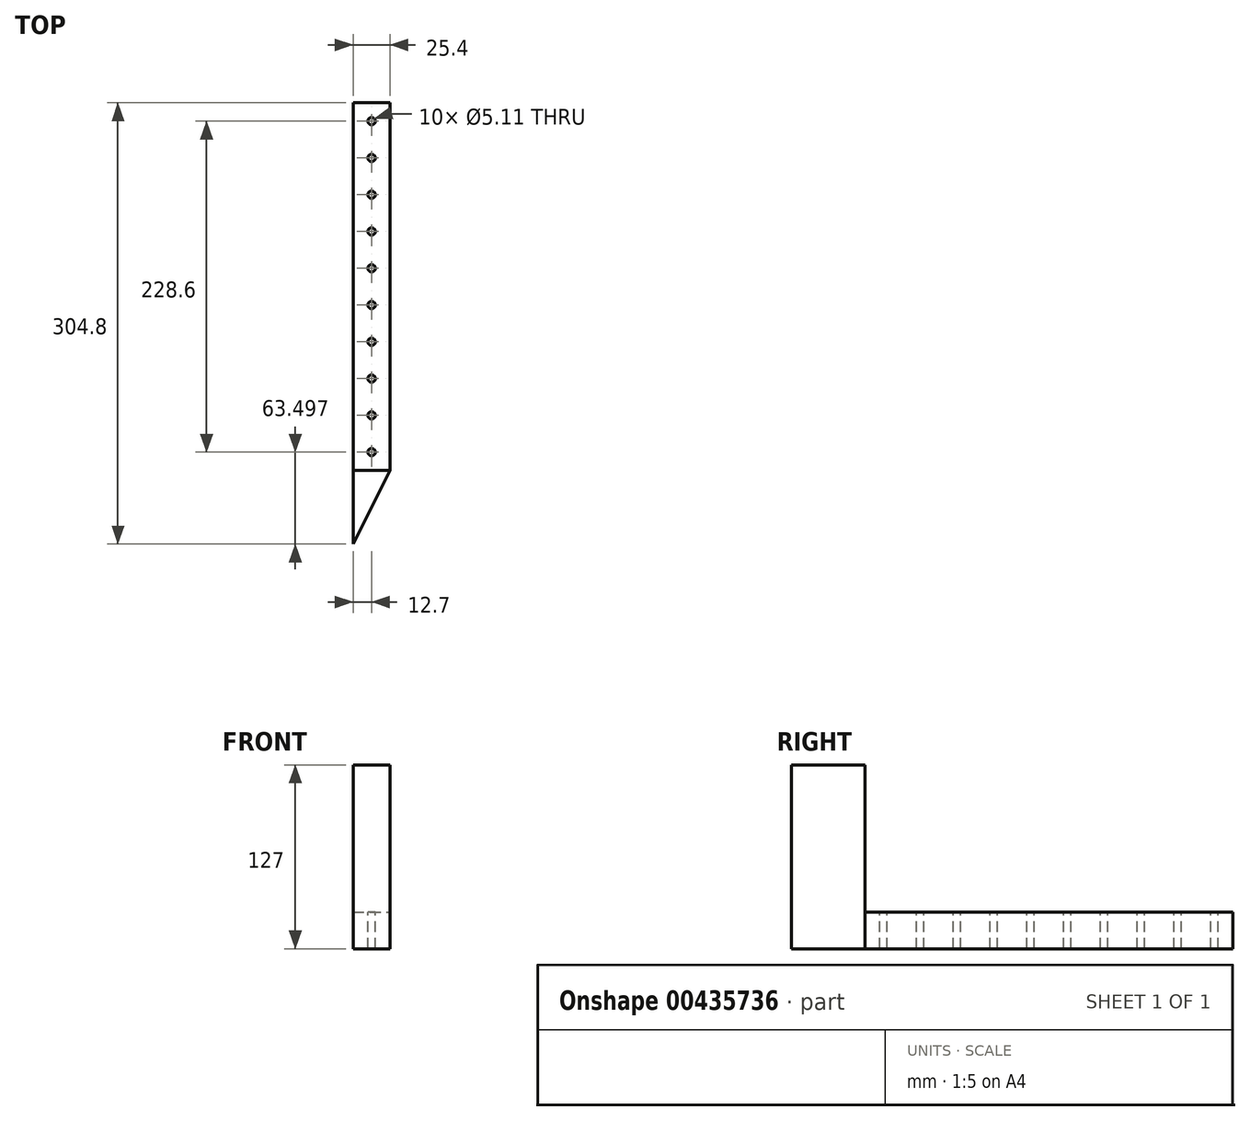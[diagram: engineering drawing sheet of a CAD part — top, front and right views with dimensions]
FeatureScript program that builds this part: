
annotation { "Feature Type Name" : "Feature", "Feature Type Description" : "" }
export const myFeature = defineFeature(function(context is Context, id is Id, definition is map)
    precondition{}
    {
        {
            var Q0;
            Q0=qCreatedBy(makeId("Top.planeOp"),FACE);
            var sketch = newSketch(context, id + "F0", { "sketchPlane" : qUnion([Q0])});
            skLineSegment(sketch, "E0.bottom", {"start": v(-56.37, 216.77) * mm, "end": v(-30.97, 216.77) * mm});
            skLineSegment(sketch, "E0.top", {"start": v(-56.37, -37.23) * mm, "end": v(-30.97, -37.23) * mm});
            skLineSegment(sketch, "E0.left", {"start": v(-56.37, 216.77) * mm, "end": v(-56.37, -37.23) * mm});
            skLineSegment(sketch, "E0.right", {"start": v(-30.97, 216.77) * mm, "end": v(-30.97, -37.23) * mm});
            skLineSegment(sketch, "E1", {"start": v(-56.37, -37.23) * mm, "end": v(-56.37, -88.03) * mm});
            skLineSegment(sketch, "E2", {"start": v(-56.37, -88.03) * mm, "end": v(-30.97, -37.23) * mm});
            skSolve(sketch);
        }
        {
            var Q0;
            Q0=makeQuery(id+"F0.imprint","IMPRINT",FACE,{"disambiguationData":[TD([[makeQuery(id+"F0.imprint","IMPRINT",EDGE,{"derivedFrom":sQuery(id+"F0.wireOp",EDGE,"E0.bottom")}),-1.0]])]});
            extrude(context, id + "F1", {"entities" : qUnion([Q0]), "depth" : 25.4 * mm});
        }
        {
            var Q0;
            Q0=makeQuery(id+"F0.imprint","IMPRINT",FACE,{"disambiguationData":[TD([[makeQuery(id+"F0.imprint","IMPRINT",EDGE,{"derivedFrom":sQuery(id+"F0.wireOp",EDGE,"E0.top")}),-1.0]])]});
            extrude(context, id + "F2", {"entities" : qUnion([Q0]), "operationType" : NewBodyOperationType.ADD, "depth" : 127 * mm});
        }
        {
            var Q0;
            Q0=makeQuery(id+"F1.opExtrude","CAP_FACE",FACE,{"disambiguationData":[OSD([sQuery(id+"F0.wireOp",EDGE,"E0.bottom"),sQuery(id+"F0.wireOp",EDGE,"E0.top"),sQuery(id+"F0.wireOp",EDGE,"E0.left"),sQuery(id+"F0.wireOp",EDGE,"E0.right")])],"isStart":false});
            var sketch = newSketch(context, id + "F3", { "sketchPlane" : qUnion([Q0])});
            skCircle(sketch, "E3", {"center": v(-43.67, 204.07) * mm, "radius": 2.55 * mm});
            skCircle(sketch, "E4.0.1.0", {"center": v(-43.67, 178.67) * mm, "radius": 2.55 * mm});
            skCircle(sketch, "E4.0.2.0", {"center": v(-43.67, 153.27) * mm, "radius": 2.55 * mm});
            skCircle(sketch, "E4.0.3.0", {"center": v(-43.67, 127.87) * mm, "radius": 2.55 * mm});
            skCircle(sketch, "E4.0.4.0", {"center": v(-43.67, 102.47) * mm, "radius": 2.55 * mm});
            skCircle(sketch, "E4.0.5.0", {"center": v(-43.67, 77.07) * mm, "radius": 2.55 * mm});
            skCircle(sketch, "E4.0.6.0", {"center": v(-43.67, 51.67) * mm, "radius": 2.55 * mm});
            skCircle(sketch, "E4.0.7.0", {"center": v(-43.67, 26.27) * mm, "radius": 2.55 * mm});
            skCircle(sketch, "E4.0.8.0", {"center": v(-43.67, 0.87) * mm, "radius": 2.55 * mm});
            skCircle(sketch, "E4.0.9.0", {"center": v(-43.67, -24.53) * mm, "radius": 2.55 * mm});
            skLineSegment(sketch, "E4.direction1", {"start": v(-43.67, 204.07) * mm, "end": v(-18.27, 204.07) * mm, "construction": true});
            skLineSegment(sketch, "E4.direction2", {"start": v(-43.67, 204.07) * mm, "end": v(-43.67, 178.67) * mm, "construction": true});
            skSolve(sketch);
        }
        {
            var Q0;
            Q0=sQuery(id+"F3.wireOp",VERTEX,"E3.center");
            var Q1;
            Q1=sQuery(id+"F3.wireOp",VERTEX,"E4.0.2.0.center");
            var Q2;
            Q2=sQuery(id+"F3.wireOp",VERTEX,"E4.0.1.0.center");
            var Q3;
            Q3=sQuery(id+"F3.wireOp",VERTEX,"E4.0.3.0.center");
            var Q4;
            Q4=sQuery(id+"F3.wireOp",VERTEX,"E4.0.4.0.center");
            var Q5;
            Q5=sQuery(id+"F3.wireOp",VERTEX,"E4.0.5.0.center");
            var Q6;
            Q6=sQuery(id+"F3.wireOp",VERTEX,"E4.0.8.0.center");
            var Q7;
            Q7=sQuery(id+"F3.wireOp",VERTEX,"E4.0.6.0.center");
            var Q8;
            Q8=sQuery(id+"F3.wireOp",VERTEX,"E4.0.7.0.center");
            var Q9;
            Q9=sQuery(id+"F3.wireOp",VERTEX,"E4.0.9.0.center");
            var Q10;
            Q10=makeQuery(id+"F1.opExtrude","SWEPT_BODY",BODY,{"disambiguationData":[OSD([sQuery(id+"F0.wireOp",EDGE,"E0.bottom"),sQuery(id+"F0.wireOp",EDGE,"E0.top"),sQuery(id+"F0.wireOp",EDGE,"E0.left"),sQuery(id+"F0.wireOp",EDGE,"E0.right")])]});
            hole(context, id + "F4", {"style" : HoleStyle.SIMPLE, "endStyle" : HoleEndStyle.THROUGH, "holeDiameter" : 5.1 * mm, "isTappedThrough" : true, "tappedDepth" : 12.7 * mm, "tapClearance" : 3, "locations" : qUnion([Q0, Q1, Q2, Q3, Q4, Q5, Q6, Q7, Q8, Q9]), "scope" : qUnion([Q10])});
        }
    });
